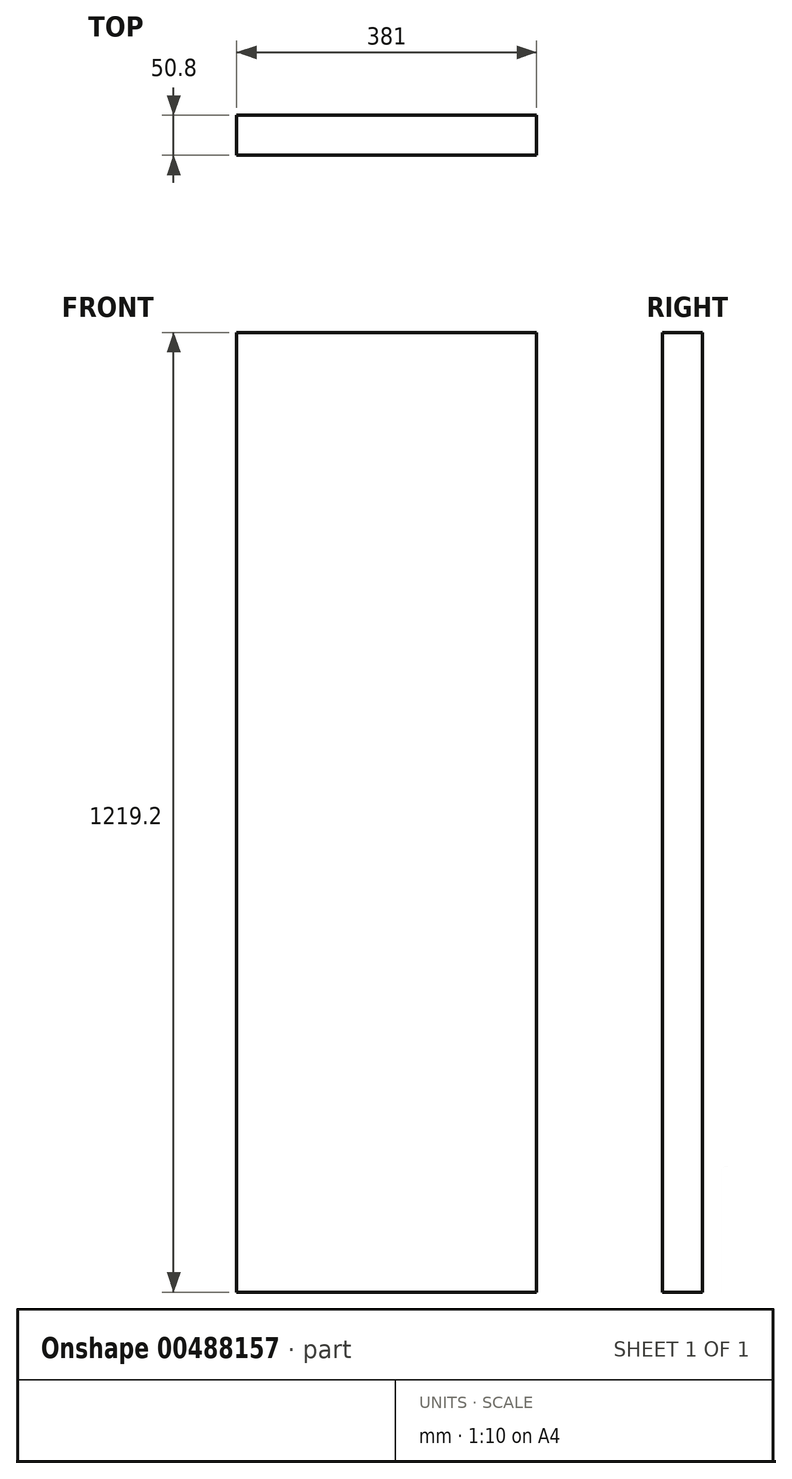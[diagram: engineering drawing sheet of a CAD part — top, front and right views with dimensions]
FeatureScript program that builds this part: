
annotation { "Feature Type Name" : "Feature", "Feature Type Description" : "" }
export const myFeature = defineFeature(function(context is Context, id is Id, definition is map)
    precondition{}
    {
        {
            var Q0;
            Q0=qCreatedBy(makeId("Front.planeOp"),FACE);
            var sketch = newSketch(context, id + "F0", { "sketchPlane" : qUnion([Q0])});
            skLineSegment(sketch, "E0", {"start": v(0, 0) * mm, "end": v(0, 0) * mm});
            skLineSegment(sketch, "E1", {"start": v(0, 0) * mm, "end": v(381, 0) * mm});
            skLineSegment(sketch, "E2", {"start": v(381, 0) * mm, "end": v(381, -1219.2) * mm});
            skLineSegment(sketch, "E3", {"start": v(381, -1219.2) * mm, "end": v(0, -1219.2) * mm});
            skLineSegment(sketch, "E4", {"start": v(0, -1219.2) * mm, "end": v(0, 0) * mm});
            skSolve(sketch);
        }
        {
            var Q0;
            Q0=makeQuery(id+"F0.imprint","IMPRINT",FACE,{"disambiguationData":[TD([[makeQuery(id+"F0.imprint","IMPRINT",EDGE,{"derivedFrom":sQuery(id+"F0.wireOp",EDGE,"E1")}),-1.0]])]});
            extrude(context, id + "F1", {"entities" : qUnion([Q0]), "depth" : 50.8 * mm, "offsetDistance" : 25.4 * mm});
        }
    });
